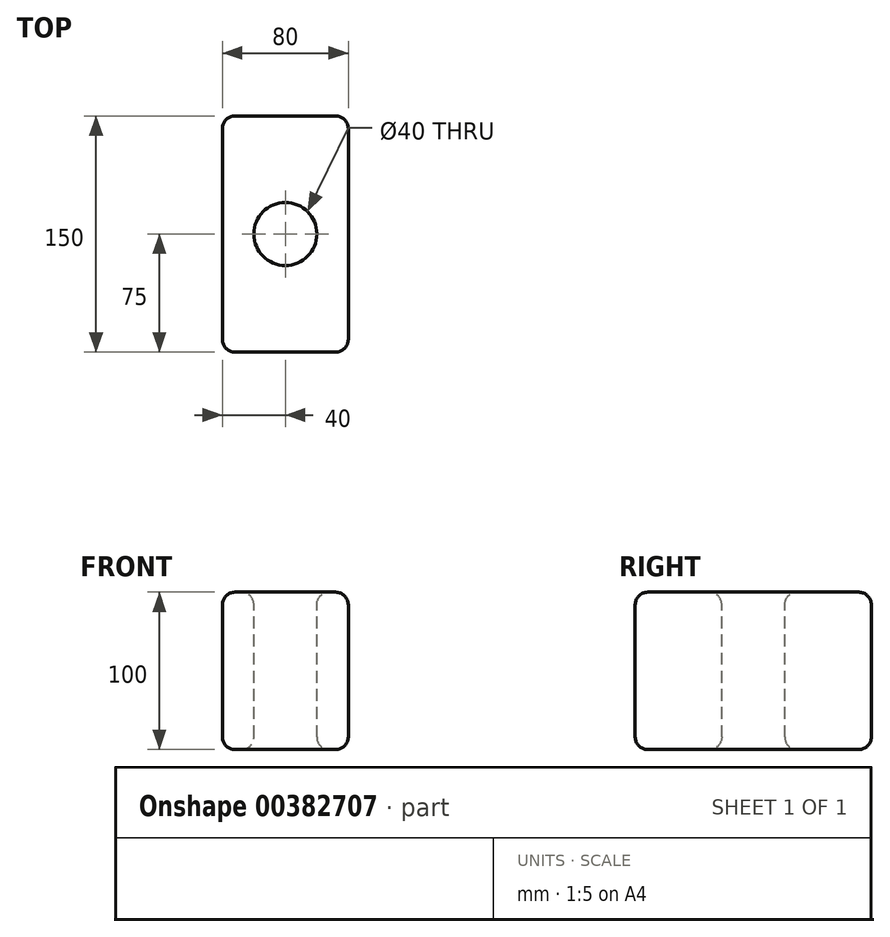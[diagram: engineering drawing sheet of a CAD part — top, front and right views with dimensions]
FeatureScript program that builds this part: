
annotation { "Feature Type Name" : "Feature", "Feature Type Description" : "" }
export const myFeature = defineFeature(function(context is Context, id is Id, definition is map)
    precondition{}
    {
        {
            var Q0;
            Q0=qCreatedBy(makeId("Front.planeOp"),FACE);
            var sketch = newSketch(context, id + "F0", { "sketchPlane" : qUnion([Q0])});
            skLineSegment(sketch, "E0.bottom", {"start": v(40, 50) * mm, "end": v(-40, 50) * mm});
            skLineSegment(sketch, "E0.top", {"start": v(40, -50) * mm, "end": v(-40, -50) * mm});
            skLineSegment(sketch, "E0.left", {"start": v(40, 50) * mm, "end": v(40, -50) * mm});
            skLineSegment(sketch, "E0.right", {"start": v(-40, 50) * mm, "end": v(-40, -50) * mm});
            skPoint(sketch, "E0.middle", {"position": v(0, 0) * mm});
            skSolve(sketch);
        }
        {
            var Q0;
            Q0 = qSketchRegion(id + "F0", true);
            extrude(context, id + "F1", {"entities" : qUnion([Q0]), "endBound" : BoundingType.SYMMETRIC, "depth" : 150 * mm});
        }
        {
            var Q0;
            Q0=makeQuery(id+"F1.opExtrude","SWEPT_FACE",FACE,{"disambiguationData":[OSD([sQuery(id+"F0.wireOp",EDGE,"E0.bottom")])]});
            var sketch = newSketch(context, id + "F2", { "sketchPlane" : qUnion([Q0])});
            skCircle(sketch, "E1", {"center": v(0, 0) * mm, "radius": 20 * mm});
            skSolve(sketch);
        }
        {
            var Q0;
            Q0 = qSketchRegion(id + "F2", true);
            extrude(context, id + "F3", {"entities" : qUnion([Q0]), "operationType" : NewBodyOperationType.REMOVE, "oppositeDirection" : true, "depth" : 107 * mm});
        }
        {
            var Q0;
            Q0=makeQuery(id+"F1.opExtrude","SWEPT_EDGE",EDGE,{"disambiguationData":[OSD([sQuery(id+"F0.wireOp",EDGE,"E0.bottom"),sQuery(id+"F0.wireOp",EDGE,"E0.left")])]});
            var Q1;
            Q1=makeQuery(id+"F1.opExtrude","CAP_FACE",FACE,{"disambiguationData":[OSD([sQuery(id+"F0.wireOp",EDGE,"E0.bottom"),sQuery(id+"F0.wireOp",EDGE,"E0.top"),sQuery(id+"F0.wireOp",EDGE,"E0.left"),sQuery(id+"F0.wireOp",EDGE,"E0.right")])],"isStart":true});
            var Q2;
            Q2=makeQuery(id+"F1.opExtrude","SWEPT_FACE",FACE,{"disambiguationData":[OSD([sQuery(id+"F0.wireOp",EDGE,"E0.right")])]});
            var Q3;
            Q3=makeQuery(id+"F1.opExtrude","CAP_FACE",FACE,{"disambiguationData":[OSD([sQuery(id+"F0.wireOp",EDGE,"E0.bottom"),sQuery(id+"F0.wireOp",EDGE,"E0.top"),sQuery(id+"F0.wireOp",EDGE,"E0.left"),sQuery(id+"F0.wireOp",EDGE,"E0.right")])],"isStart":false});
            var Q4;
            Q4=makeQuery(id+"F1.opExtrude","SWEPT_FACE",FACE,{"disambiguationData":[OSD([sQuery(id+"F0.wireOp",EDGE,"E0.left")])]});
            var Q5;
            Q5=makeQuery(id+"F1.opExtrude","SWEPT_FACE",FACE,{"disambiguationData":[OSD([sQuery(id+"F0.wireOp",EDGE,"E0.top")])]});
            var Q6;
            Q6=makeQuery(id+"F1.opExtrude","SWEPT_FACE",FACE,{"disambiguationData":[OSD([sQuery(id+"F0.wireOp",EDGE,"E0.bottom")])]});
            fillet(context, id + "F4", {"entities" : qUnion([Q0, Q1, Q2, Q3, Q4, Q5, Q6]), "radius" : 8 * mm, "tangentPropagation" : true, "allowEdgeOverflow" : false});
        }
    });
